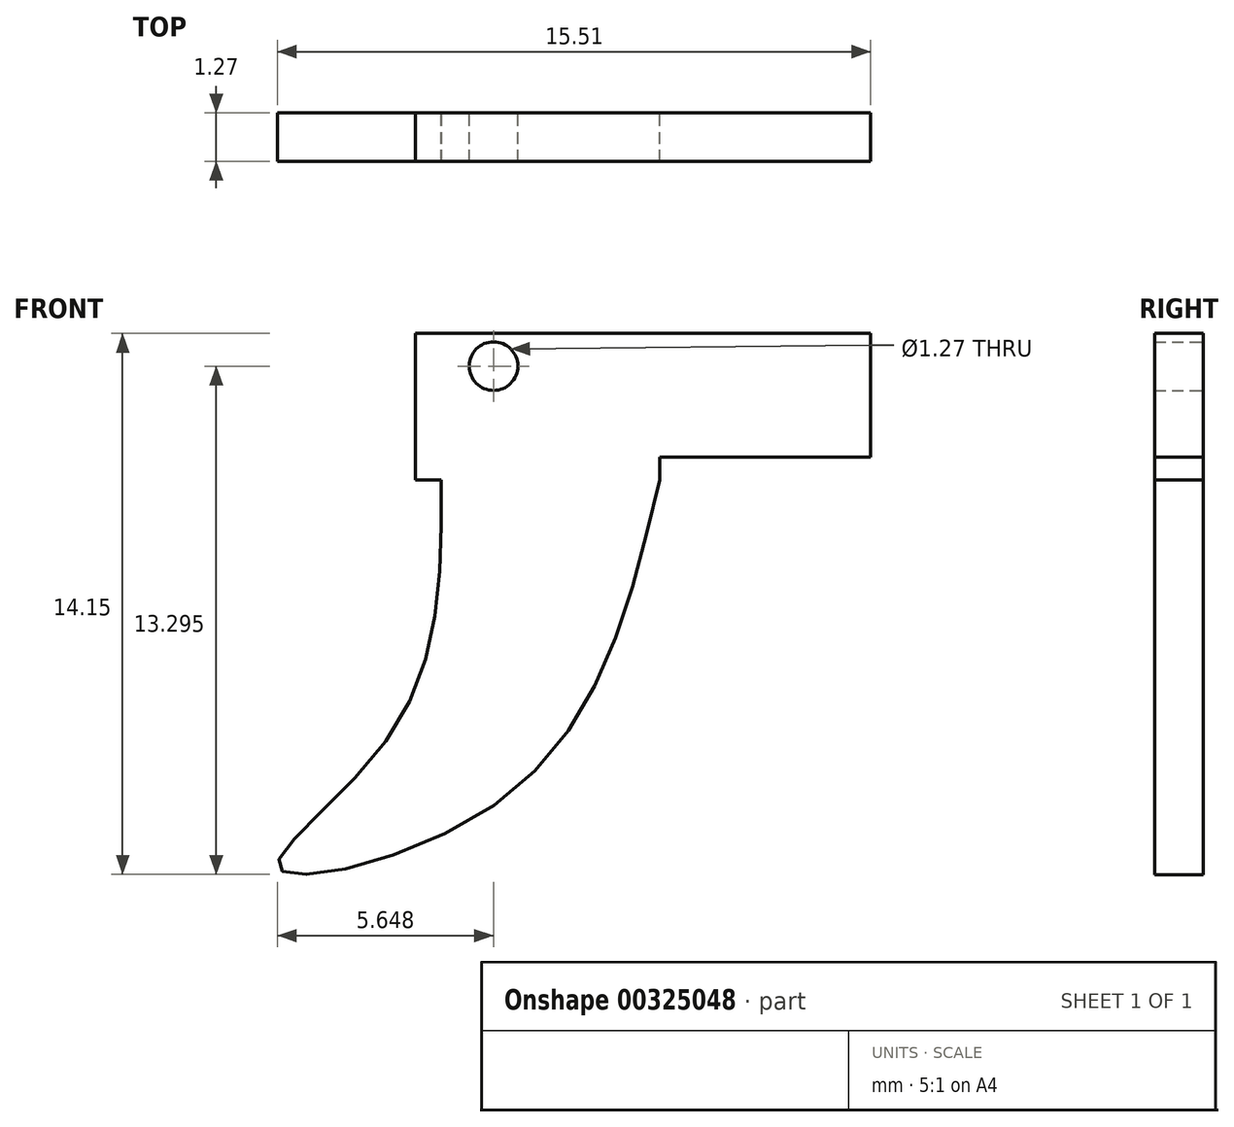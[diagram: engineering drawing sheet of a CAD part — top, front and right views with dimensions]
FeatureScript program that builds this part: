
annotation { "Feature Type Name" : "Feature", "Feature Type Description" : "" }
export const myFeature = defineFeature(function(context is Context, id is Id, definition is map)
    precondition{}
    {
        {
            var Q0;
            Q0=qCreatedBy(makeId("Front.planeOp"),FACE);
            var sketch = newSketch(context, id + "F0", { "sketchPlane" : qUnion([Q0])});
            skLineSegment(sketch, "E0.bottom", {"start": v(14.01, 19.86) * mm, "end": v(20.4, 19.86) * mm});
            skLineSegment(sketch, "E0.top", {"start": v(14.01, 16.03) * mm, "end": v(20.4, 16.03) * mm});
            skLineSegment(sketch, "E0.left", {"start": v(14.01, 19.86) * mm, "end": v(14.01, 16.03) * mm});
            skLineSegment(sketch, "E0.right", {"start": v(20.4, 19.86) * mm, "end": v(20.4, 16.03) * mm});
            skLineSegment(sketch, "E1", {"start": v(14.01, 19) * mm, "end": v(16.05, 19) * mm});
            skFitSpline(sketch, "E2", {"points": [v(14.68, 16.03) * mm, v(13.34, 9.35) * mm, v(10.43, 5.88) * mm, v(16.22, 7.63) * mm, v(20.4, 16.03) * mm], "startDerivative": vector(0.18, -27.65) * mm, "endDerivative": vector(7.63, 32.5) * mm});
            skLineSegment(sketch, "E3.bottom", {"start": v(20.4, 19.86) * mm, "end": v(25.91, 19.86) * mm});
            skLineSegment(sketch, "E3.top", {"start": v(20.4, 16.62) * mm, "end": v(25.91, 16.62) * mm});
            skLineSegment(sketch, "E3.left", {"start": v(20.4, 19.86) * mm, "end": v(20.4, 16.62) * mm});
            skLineSegment(sketch, "E3.right", {"start": v(25.91, 19.86) * mm, "end": v(25.91, 16.62) * mm});
            skSolve(sketch);
        }
        {
            var Q0;
            Q0 = qSketchRegion(id + "F0", true);
            extrude(context, id + "F1", {"entities" : qUnion([Q0]), "depth" : 1.27 * mm});
        }
        {
            var Q0;
            Q0=sQuery(id+"F0.wireOp",VERTEX,"E1.end");
            var Q1;
            Q1=makeQuery(id+"F1.opExtrude","SWEPT_BODY",BODY,{"disambiguationData":[OSD([sQuery(id+"F0.wireOp",EDGE,"E0.bottom"),sQuery(id+"F0.wireOp",EDGE,"E0.top"),sQuery(id+"F0.wireOp",EDGE,"E0.left"),sQuery(id+"F0.wireOp",EDGE,"E0.right"),sQuery(id+"F0.wireOp",EDGE,"28712f01-9425-4136-a201-cf3976387fa9")])]});
            hole(context, id + "F2", {"style" : HoleStyle.SIMPLE, "endStyle" : HoleEndStyle.THROUGH, "oppositeDirection" : true, "holeDiameter" : 1.27 * mm, "tappedDepth" : 12.7 * mm, "tapClearance" : 3, "locations" : qUnion([Q0]), "scope" : qUnion([Q1])});
        }
    });
